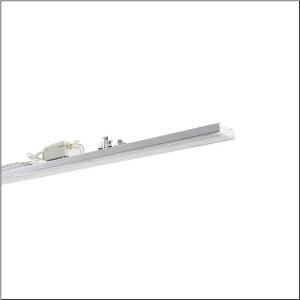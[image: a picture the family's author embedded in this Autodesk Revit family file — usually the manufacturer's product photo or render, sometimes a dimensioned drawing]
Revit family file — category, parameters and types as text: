
# Revit family: licross_r__21_recessed_ho_52te12dn4fxm3s_1d6f
name_source: partatom
category: Lighting Fixtures
units: mm (PartAtom-declared; Revit-internal decimal feet)

## family parameters
Cut with Voids When Loaded = No
Host = Face
Light Source = No
Part Type = Normal
Room Calculation Point = No
Round Connector Dimension = Use Diameter
Shared = No

## types (1)
- --- (1 x LED, 930 lm, 7.5 W, 4000K)
    Apparent Load = 8 VA
    CIE Flux Codes = 69 91 98 100 100
    Color Rendering = 80
    Color Temperature = 4000K
    Default Elevation = 1800 mm
    Description = Licross® 21 Recessed HO, luminaire insert, of sheet steel, galvanised, coil coated, white, length: 1.500mm, width: 66mm, height: 67mm, LED rated luminous flux: 15.000lm, light colour: 840, control gear: DALI 2, with plug, 6-pole, with phase selection, for trunking rail, 14-core, mains connection: 220..240V, AC, 50/60Hz, rated input power: 88W, halogen-free wiring, for emergency light function, for trunking rail, 14-core, converter,control gear: single battery element, battery: LiFeP04, 9Ah, primary optical cover: cover, of PMMA, light emission: direct distribution, primary light characteristic: symmetric, protection rating (complete): IP54, insulation class (complete): insulation class I (protective earthing), certification: CE, UKCA, protection symbol: D if used in an environment with non-conductive dust loads with corresponding accessories, impact resistance: IK06, permissible ambient temperature for indoor applications: +5..+30°C, standard: EN 60598-2-22, LABS conformity tested according to VDMA 24364:2018-05, reducing of maximum allowable ambient temperature of 5°C with ceiling mounting, corresponds to IFS (International Featured Standards) requirements for safety and quality in the food industry, packaging unit: 1 piece
    Height = 58 mm
    Lamp = 1 x LED
    Lamp Light Flux = 930 lm
    Lamp Power = 7.5 W
    Lamp count = 1
    Length = 1500 mm
    Luminous efficacy = 124 lm/W
    Manufacturer = Siteco
    ModVariant = No
    Model = 52TE12DN4FXM3S
    Mounting Place = Ceiling
    Mounting Type = Pendant
    Number of Poles = 1
    OnlyDefault = Yes
    Power Factor = 1
    Product Name = Licross® 21 Recessed HO
    Product group = luminaire insert
    ProductGroupID = 901
    Protection Class = Protection class I
    Protection Degree = IP 54
    RLX_Detail_Level = 1
    RLX_Emergency_Light_Flux = 0 lm
    RLX_Emergency_Type = 0
    RLX_Emergency_Type_DB = No
    RlxData = <blob elided: 25089 chars, md5=6d333f1e>
    Socket = socket
    Standby Power = 0 W
    System Light Flux = 930 lm
    System Power = 8 W
    Type Comments = : emergency light operation: 3 h
    Type Image = l_1296930.jpg
    URL = http://relux.com
    VarID = @adj_039449
    Voltage = 0 V
    Weight = 0.00 kg
    Width = 66 mm

## geometry (parser evidence)
native form markers: Blend x4, Sweep x11
no freeform markers — native parametric forms only
